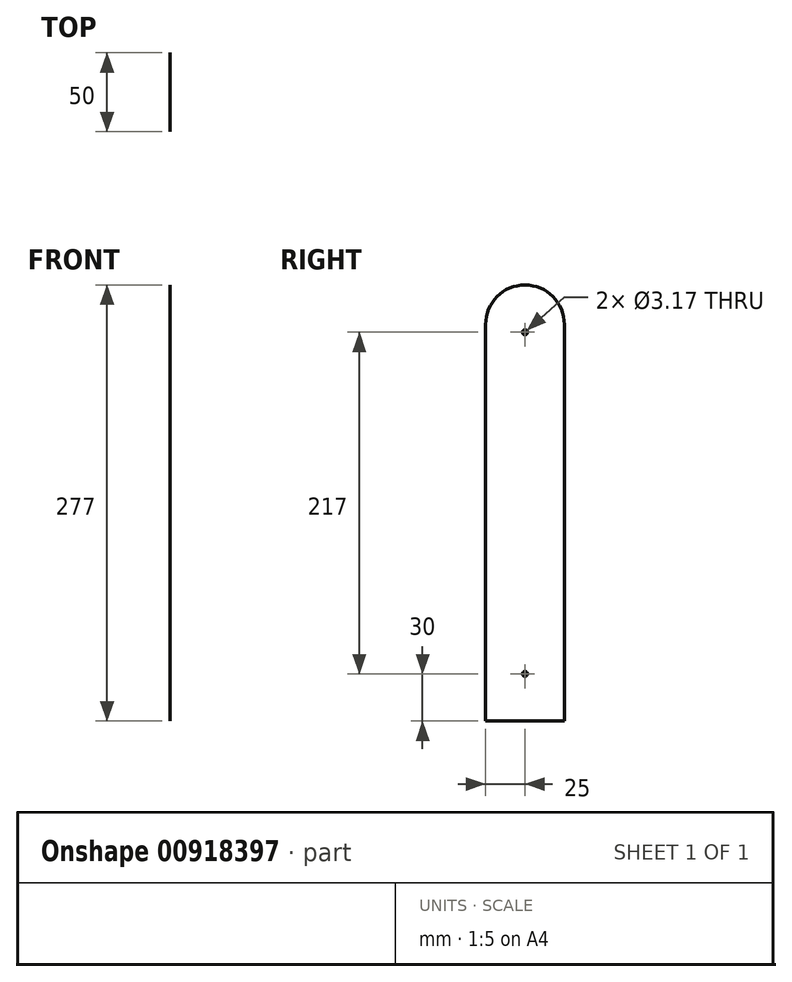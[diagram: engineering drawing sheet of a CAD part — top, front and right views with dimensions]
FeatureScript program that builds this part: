
annotation { "Feature Type Name" : "Feature", "Feature Type Description" : "" }
export const myFeature = defineFeature(function(context is Context, id is Id, definition is map)
    precondition{}
    {
        {
            assignVariable(context, id + "F0", {"name" : "Thickness", "anyValue" : 1 / 203.2 * mm});
        }
        {
            var Q0;
            Q0=qCreatedBy(makeId("Right.planeOp"),FACE);
            var sketch = newSketch(context, id + "F1", { "sketchPlane" : qUnion([Q0])});
            skLineSegment(sketch, "E0.bottom", {"start": v(25, 138.5) * mm, "end": v(-25, 138.5) * mm});
            skLineSegment(sketch, "E0.top", {"start": v(25, -138.5) * mm, "end": v(-25, -138.5) * mm});
            skLineSegment(sketch, "E0.left", {"start": v(25, 138.5) * mm, "end": v(25, -138.5) * mm});
            skLineSegment(sketch, "E0.right", {"start": v(-25, 138.5) * mm, "end": v(-25, -138.5) * mm});
            skPoint(sketch, "E0.middle", {"position": v(0, 0) * mm});
            skCircle(sketch, "E1", {"center": v(0, 108.5) * mm, "radius": 1.59 * mm});
            skCircle(sketch, "E2", {"center": v(0, -108.5) * mm, "radius": 1.59 * mm});
            skLineSegment(sketch, "E3", {"start": v(0, 138.5) * mm, "end": v(0, 108.5) * mm, "construction": true});
            skLineSegment(sketch, "E4", {"start": v(0, 108.5) * mm, "end": v(0, -108.5) * mm, "construction": true});
            skLineSegment(sketch, "E5", {"start": v(0, -108.5) * mm, "end": v(0, -138.5) * mm, "construction": true});
            skSolve(sketch);
        }
        {
            var Q0;
            Q0=makeQuery(id+"F1.imprint","IMPRINT",FACE,{"disambiguationData":[TD([[makeQuery(id+"F1.imprint","IMPRINT",EDGE,{"derivedFrom":sQuery(id+"F1.wireOp",EDGE,"E0.bottom")}),1.0]])]});
            extrude(context, id + "F2", {"entities" : qUnion([Q0]), "depth" : getVariable(context, 'Thickness'), "offsetDistance" : 25 * mm, "symmetric" : true});
        }
        {
            var Q0;
            Q0=makeQuery(id+"F2.opExtrude","SWEPT_EDGE",EDGE,{"disambiguationData":[OSD([sQuery(id+"F1.wireOp",EDGE,"E0.bottom"),sQuery(id+"F1.wireOp",EDGE,"E0.right")])]});
            var Q1;
            Q1=makeQuery(id+"F2.opExtrude","SWEPT_EDGE",EDGE,{"disambiguationData":[OSD([sQuery(id+"F1.wireOp",EDGE,"E0.bottom"),sQuery(id+"F1.wireOp",EDGE,"E0.left")])]});
            fillet(context, id + "F3", {"entities" : qUnion([Q0, Q1]), "radius" : 25 * mm, "tangentPropagation" : true, "allowEdgeOverflow" : false});
        }
    });
